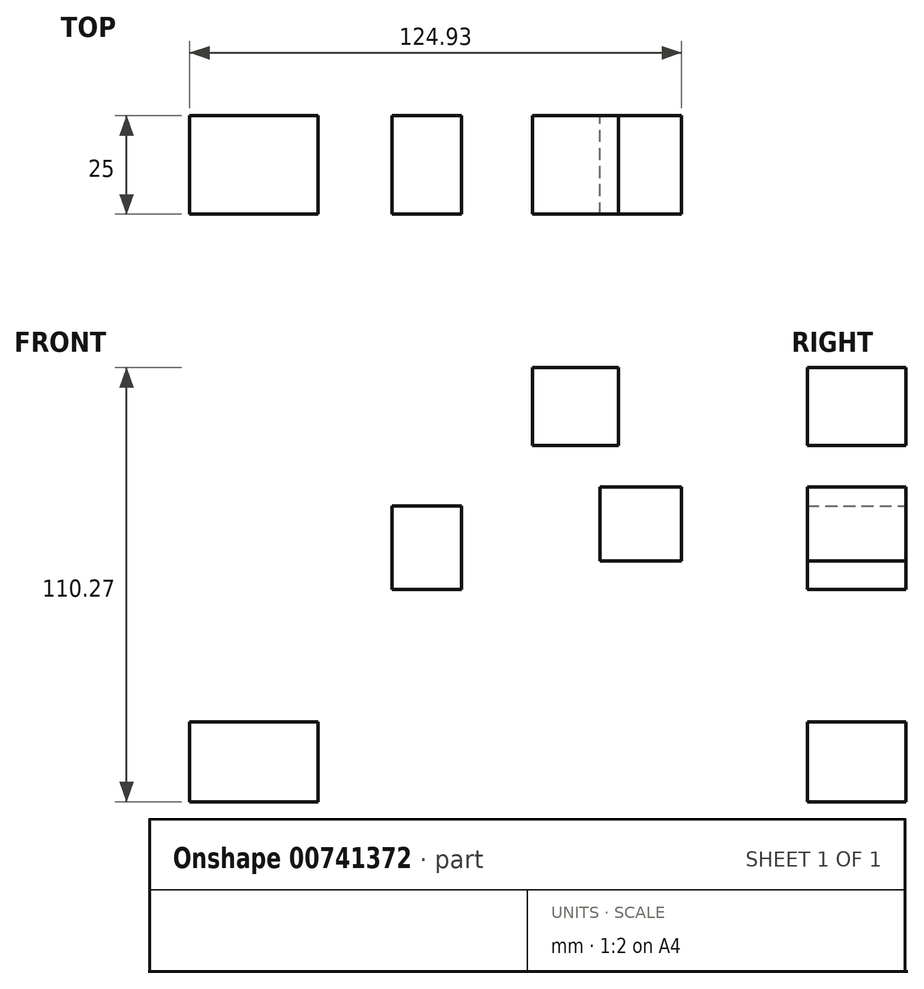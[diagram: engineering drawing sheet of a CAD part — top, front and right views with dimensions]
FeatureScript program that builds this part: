
annotation { "Feature Type Name" : "Feature", "Feature Type Description" : "" }
export const myFeature = defineFeature(function(context is Context, id is Id, definition is map)
    precondition{}
    {
        {
            var Q0;
            Q0=qCreatedBy(makeId("Front.planeOp"),FACE);
            var sketch = newSketch(context, id + "F0", { "sketchPlane" : qUnion([Q0])});
            skLineSegment(sketch, "E0.bottom", {"start": v(14.5, 4.84) * mm, "end": v(35.25, 4.84) * mm});
            skLineSegment(sketch, "E0.top", {"start": v(14.5, -13.95) * mm, "end": v(35.25, -13.95) * mm});
            skLineSegment(sketch, "E0.left", {"start": v(14.5, 4.84) * mm, "end": v(14.5, -13.95) * mm});
            skLineSegment(sketch, "E0.right", {"start": v(35.25, 4.84) * mm, "end": v(35.25, -13.95) * mm});
            skLineSegment(sketch, "E1.bottom", {"start": v(-20.63, 0) * mm, "end": v(-38.21, 0) * mm});
            skLineSegment(sketch, "E1.top", {"start": v(-20.63, -21.23) * mm, "end": v(-38.21, -21.23) * mm});
            skLineSegment(sketch, "E1.left", {"start": v(-20.63, 0) * mm, "end": v(-20.63, -21.23) * mm});
            skLineSegment(sketch, "E1.right", {"start": v(-38.21, 0) * mm, "end": v(-38.21, -21.23) * mm});
            skLineSegment(sketch, "E2.bottom", {"start": v(-89.68, -54.81) * mm, "end": v(-57.1, -54.81) * mm});
            skLineSegment(sketch, "E2.top", {"start": v(-89.68, -75.13) * mm, "end": v(-57.1, -75.13) * mm});
            skLineSegment(sketch, "E2.left", {"start": v(-89.68, -54.81) * mm, "end": v(-89.68, -75.13) * mm});
            skLineSegment(sketch, "E2.right", {"start": v(-57.1, -54.81) * mm, "end": v(-57.1, -75.13) * mm});
            skLineSegment(sketch, "E3.bottom", {"start": v(19.32, 35.14) * mm, "end": v(-2.58, 35.14) * mm});
            skLineSegment(sketch, "E3.top", {"start": v(19.32, 15.38) * mm, "end": v(-2.58, 15.38) * mm});
            skLineSegment(sketch, "E3.left", {"start": v(19.32, 35.14) * mm, "end": v(19.32, 15.38) * mm});
            skLineSegment(sketch, "E3.right", {"start": v(-2.58, 35.14) * mm, "end": v(-2.58, 15.38) * mm});
            skSolve(sketch);
        }
        {
            var Q0;
            Q0 = qSketchRegion(id + "F0", true);
            extrude(context, id + "F1", {"entities" : qUnion([Q0]), "depth" : 25 * mm, "offsetDistance" : 25 * mm});
        }
    });
